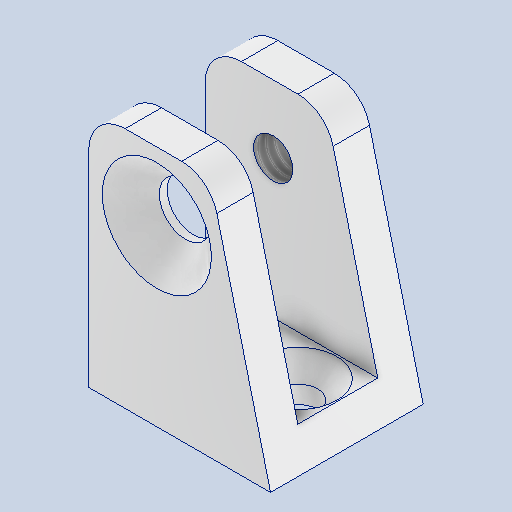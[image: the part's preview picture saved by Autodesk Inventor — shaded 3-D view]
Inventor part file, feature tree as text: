
AUTODESK INVENTOR PART (.ipt)
format: ipt  version: 2025 (Build 290162010, 162A)  size: 216,064 bytes
history: native  units: mm
features: sketch x5, hole x3, extrude x2, chamfer x2, fillet x1
ambient origin geometry x8: Origin, YZ Plane, XZ Plane, XY Plane, X Axis, Y Axis, Z Axis, Center Point
bodies: Volumenkörper1 (feature_tree)
feature tree (13):
  extrude  "Extrusion1"  Depth=3.0mm
  chamfer  "Fasen1"  Distance=20.0mm
  chamfer  "Fasen2"  Distance=20.0mm
  fillet  "Rundung1"  Radius=5.0mm
  hole  "Bohrung1"  [1 undecoded]
  extrude  "Extrusion2"  Depth=8.0mm
  hole  "Bohrung2"  [1 undecoded]
  hole  "Bohrung3"  [1 undecoded]
  sketch  "Skizze1"  dims[d0=15.0mm d1=3.0mm]
  sketch  "Skizze2"  dims[d2=3.0mm]
  sketch  "Skizze3"  dims[d3=6.6mm d5=20.0mm d6=0.0mm]
  sketch  "Skizze4"  dims[d7=3.0mm]
  sketch  "Skizze5"  dims[d8=3.242mm d9=8.0mm d10=9.0mm d11=14.0mm d12=90.0deg d13=11.8mm d14=20.594885mm d16=20.0mm d17=0.0mm d19=3.2mm d20=8.0mm d21=6.3mm d22=2.0mm d23=90.0deg d24=8.0mm d25=20.594885mm d26=4.3mm d27=8.0mm d28=4.0mm d29=2.0mm d30=90.0deg d31=5.0mm d32=20.594885mm d42=5.0mm d43=20.0mm d44=45.0deg d45=5.0mm d46=20.0mm d47=45.0deg d48=8.0mm d49=3.0mm d50=3.25mm d51=3.0mm]
note: 3 required parameter values undecoded (feature->parameter linkage not recoverable at this tier; creation-order binding heuristic only, values carry confidence <= 0.55)
